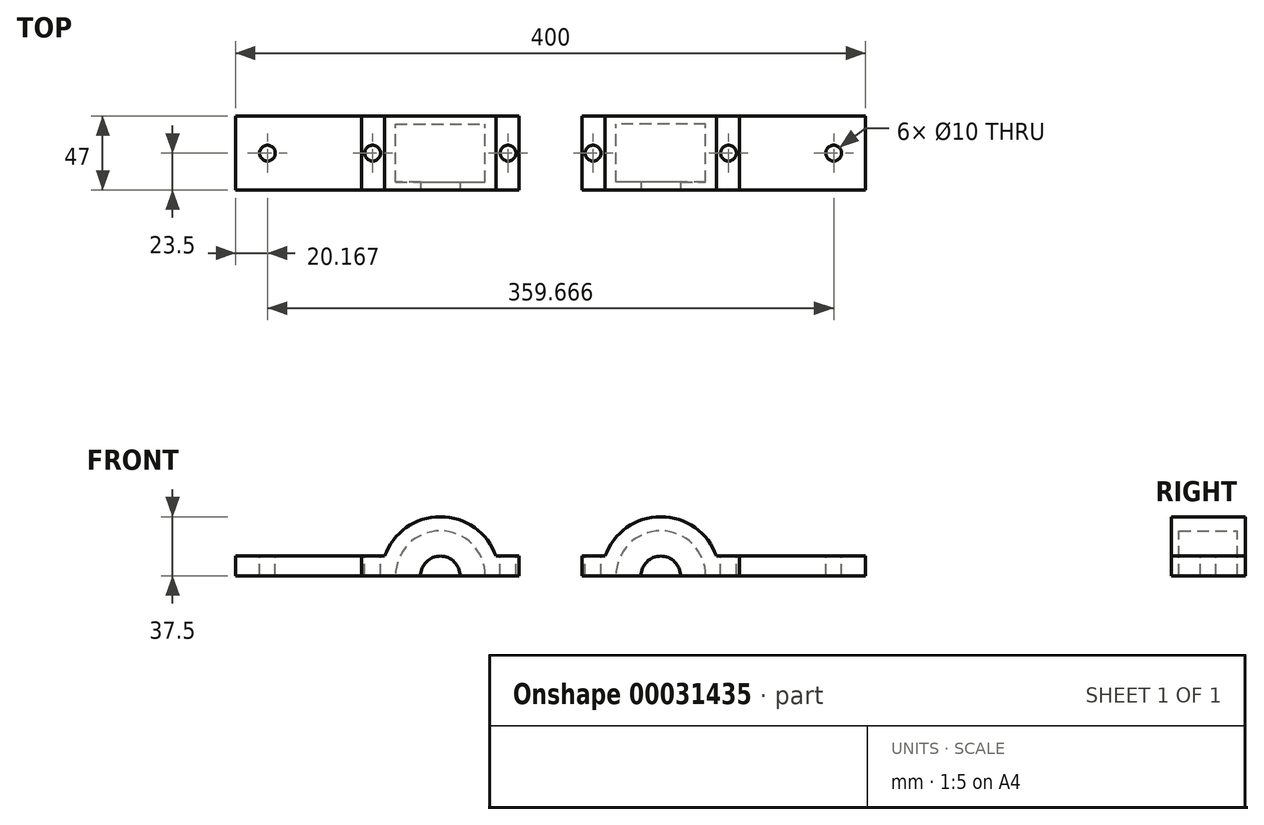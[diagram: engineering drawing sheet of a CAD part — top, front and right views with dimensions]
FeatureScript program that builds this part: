
annotation { "Feature Type Name" : "Feature", "Feature Type Description" : "" }
export const myFeature = defineFeature(function(context is Context, id is Id, definition is map)
    precondition{}
    {
        {
            var Q0;
            Q0=qCreatedBy(makeId("Front.planeOp"),FACE);
            var sketch = newSketch(context, id + "F0", { "sketchPlane" : qUnion([Q0])});
            skLineSegment(sketch, "E0.bottom", {"start": v(0, 0) * mm, "end": v(-50, 0) * mm});
            skLineSegment(sketch, "E0.top", {"start": v(0, 50) * mm, "end": v(-50, 50) * mm});
            skLineSegment(sketch, "E0.left", {"start": v(0, 0) * mm, "end": v(0, 50) * mm});
            skLineSegment(sketch, "E0.right", {"start": v(-50, 0) * mm, "end": v(-50, 50) * mm});
            skArc(sketch, "E1", {"start": v(0, 28.5) * mm, "mid": v(-20.15, 20.15) * mm, "end": v(-28.5, 0) * mm});
            skSolve(sketch);
        }
        {
            var Q0;
            {var subQ3=sQuery(id+"F0.wireOp",EDGE,"E0.top");Q0=makeQuery(id+"F0.imprint","IMPRINT",FACE,{"disambiguationData":[TD([[makeQuery(id+"F0.imprint","IMPRINT",EDGE,{"derivedFrom":subQ3}),1.0]])]});}
            extrude(context, id + "F1", {"entities" : qUnion([Q0]), "depth" : 37 * mm});
        }
        {
            var Q0;
            {var subQ0=sQuery(id+"F0.wireOp",EDGE,"E1");Q0=makeQuery(id+"F0.imprint","IMPRINT",FACE,{"disambiguationData":[TD([[makeQuery(id+"F0.imprint","IMPRINT",EDGE,{"derivedFrom":subQ0}),1.0]])]});}
            var Q1;
            {var subQ3=sQuery(id+"F0.wireOp",EDGE,"E0.top");Q1=makeQuery(id+"F0.imprint","IMPRINT",FACE,{"disambiguationData":[TD([[makeQuery(id+"F0.imprint","IMPRINT",EDGE,{"derivedFrom":subQ3}),1.0]])]});}
            extrude(context, id + "F2", {"entities" : qUnion([Q0, Q1]), "operationType" : NewBodyOperationType.ADD, "oppositeDirection" : true, "depth" : 5 * mm});
        }
        {
            var Q0;
            Q0=qCreatedBy(makeId("Front.planeOp"),FACE);
            cPlane(context, id + "F3", {"entities" : qUnion([Q0]), "cplaneType" : CPlaneType.OFFSET, "offset" : 37 * mm, "width" : 150 * mm, "height" : 150 * mm});
        }
        {
            var Q0;
            Q0=qCreatedBy(id+"F3.planeOp",FACE);
            var sketch = newSketch(context, id + "F4", { "sketchPlane" : qUnion([Q0])});
            skLineSegment(sketch, "E2.bottom", {"start": v(0, 0) * mm, "end": v(-50, 0) * mm});
            skLineSegment(sketch, "E2.top", {"start": v(0, 50) * mm, "end": v(-50, 50) * mm});
            skLineSegment(sketch, "E2.left", {"start": v(0, 0) * mm, "end": v(0, 50) * mm});
            skLineSegment(sketch, "E2.right", {"start": v(-50, 0) * mm, "end": v(-50, 50) * mm});
            skSolve(sketch);
        }
        {
            var Q0;
            Q0 = qSketchRegion(id + "F4", true);
            extrude(context, id + "F5", {"entities" : qUnion([Q0]), "depth" : 5 * mm});
        }
        {
            var Q0;
            Q0=makeQuery(id+"F1.opExtrude","SWEPT_BODY",BODY,{"disambiguationData":[OSD([sQuery(id+"F0.wireOp",EDGE,"E0.bottom"),sQuery(id+"F0.wireOp",EDGE,"E0.top"),sQuery(id+"F0.wireOp",EDGE,"E0.left"),sQuery(id+"F0.wireOp",EDGE,"E0.right"),sQuery(id+"F0.wireOp",EDGE,"E1")])]});
            var Q1;
            Q1=makeQuery(id+"F5.opExtrude","SWEPT_BODY",BODY,{"disambiguationData":[OSD([sQuery(id+"F4.wireOp",EDGE,"E2.bottom"),sQuery(id+"F4.wireOp",EDGE,"E2.top"),sQuery(id+"F4.wireOp",EDGE,"E2.left"),sQuery(id+"F4.wireOp",EDGE,"E2.right")])]});
            booleanBodies(context, id + "F6", {"operationType" : BooleanOperationType.UNION, "tools" : qUnion([Q0, Q1])});
        }
        {
            var Q0;
            {var subQ0=sQuery(id+"F0.wireOp",EDGE,"E0.top");var subQ1=makeQuery(id+"F2.boolean.opBoolean","MERGE",FACE,{"derivedFrom":[makeQuery(id+"F1.opExtrude","SWEPT_FACE",FACE,{"disambiguationData":[OSD([subQ0])]}),makeQuery(id+"F2.opExtrude","SWEPT_FACE",FACE,{"disambiguationData":[OSD([subQ0])]})]});var subQ2=makeQuery(id+"F5.opExtrude","SWEPT_FACE",FACE,{"disambiguationData":[OSD([sQuery(id+"F4.wireOp",EDGE,"E2.top")])]});Q0=makeQuery(id+"F6.opBoolean","MERGE",FACE,{"derivedFrom":[makeQuery(id+"FJoy3nQs1lwyxgx_1.boolean.opBoolean","MERGE",FACE,{"derivedFrom":[subQ1,makeQuery(id+"FJoy3nQs1lwyxgx_1.opPattern","COPY",FACE,{"derivedFrom":subQ1,"instanceName":"1"})]}),makeQuery(id+"Fkg0O5OeTg1i3LZ_2.boolean.opBoolean","MERGE",FACE,{"derivedFrom":[subQ2,makeQuery(id+"Fkg0O5OeTg1i3LZ_2.opPattern","COPY",FACE,{"derivedFrom":subQ2,"instanceName":"1"})]})]});}
            var sketch = newSketch(context, id + "F7", { "sketchPlane" : qUnion([Q0])});
            skCircle(sketch, "E3", {"center": v(-43, -18.5) * mm, "radius": 5 * mm});
            skSolve(sketch);
        }
        {
            var Q0;
            Q0 = qSketchRegion(id + "F7", true);
            extrude(context, id + "F8", {"entities" : qUnion([Q0]), "operationType" : NewBodyOperationType.REMOVE, "oppositeDirection" : true, "depth" : 100 * mm});
        }
        {
            var Q0;
            Q0=makeQuery(id+"F5.opExtrude","CAP_FACE",FACE,{"disambiguationData":[OSD([sQuery(id+"F4.wireOp",EDGE,"E2.bottom"),sQuery(id+"F4.wireOp",EDGE,"E2.top"),sQuery(id+"F4.wireOp",EDGE,"E2.left"),sQuery(id+"F4.wireOp",EDGE,"E2.right")])],"isStart":false});
            var sketch = newSketch(context, id + "F9", { "sketchPlane" : qUnion([Q0])});
            skCircle(sketch, "E4", {"center": v(0, 0) * mm, "radius": 12.5 * mm});
            skSolve(sketch);
        }
        {
            var Q0;
            Q0 = qSketchRegion(id + "F9", true);
            extrude(context, id + "F10", {"entities" : qUnion([Q0]), "operationType" : NewBodyOperationType.REMOVE, "oppositeDirection" : true, "depth" : 5 * mm});
        }
        {
            var Q0;
            Q0=makeQuery(id+"F5.opExtrude","CAP_FACE",FACE,{"disambiguationData":[OSD([sQuery(id+"F4.wireOp",EDGE,"E2.bottom"),sQuery(id+"F4.wireOp",EDGE,"E2.top"),sQuery(id+"F4.wireOp",EDGE,"E2.left"),sQuery(id+"F4.wireOp",EDGE,"E2.right")])],"isStart":false});
            var sketch = newSketch(context, id + "F11", { "sketchPlane" : qUnion([Q0])});
            skLineSegment(sketch, "E5", {"start": v(0, 12.5) * mm, "end": v(-50, 12.5) * mm, "construction": true});
            skCircle(sketch, "E6", {"center": v(0, 0) * mm, "radius": 37.5 * mm});
            skLineSegment(sketch, "E7", {"start": v(-25, 12.5) * mm, "end": v(-50, 12.5) * mm});
            skLineSegment(sketch, "E8", {"start": v(-50, 50) * mm, "end": v(0, 50) * mm});
            skLineSegment(sketch, "E9", {"start": v(0, 50) * mm, "end": v(0, 37.5) * mm});
            skPoint(sketch, "E9.endSnap0", {"position": v(0, 31.25) * mm});
            skLineSegment(sketch, "E10", {"start": v(-35.36, 12.5) * mm, "end": v(-25, 12.5) * mm});
            skSolve(sketch);
        }
        {
            var Q0;
            {var subQ1=sQuery(id+"F11.wireOp",EDGE,"E7");Q0=makeQuery(id+"F11.imprint","IMPRINT",FACE,{"disambiguationData":[TD([[makeQuery(id+"F11.imprint","IMPRINT",EDGE,{"derivedFrom":subQ1}),-1.0]])]});}
            extrude(context, id + "F12", {"entities" : qUnion([Q0]), "operationType" : NewBodyOperationType.REMOVE, "oppositeDirection" : true, "depth" : 55 * mm});
        }
        {
            var Q0;
            Q0=makeQuery(id+"F1.opExtrude","SWEPT_BODY",BODY,{"disambiguationData":[OSD([sQuery(id+"F0.wireOp",EDGE,"E0.bottom"),sQuery(id+"F0.wireOp",EDGE,"E0.top"),sQuery(id+"F0.wireOp",EDGE,"E0.left"),sQuery(id+"F0.wireOp",EDGE,"E0.right"),sQuery(id+"F0.wireOp",EDGE,"E1")])]});
            var Q1;
            Q1=qCreatedBy(makeId("Right.planeOp"),FACE);
            mirror(context, id + "F13", {"operationType" : NewBodyOperationType.ADD, "entities" : qUnion([Q0]), "mirrorPlane" : qUnion([Q1])});
        }
        {
            var Q0;
            {var subQ0=makeQuery(id+"F5.opExtrude","CAP_FACE",FACE,{"disambiguationData":[OSD([sQuery(id+"F4.wireOp",EDGE,"E2.bottom"),sQuery(id+"F4.wireOp",EDGE,"E2.top"),sQuery(id+"F4.wireOp",EDGE,"E2.left"),sQuery(id+"F4.wireOp",EDGE,"E2.right")])],"isStart":false});Q0=makeQuery(id+"F13.boolean.opBoolean","MERGE",FACE,{"derivedFrom":[subQ0,makeQuery(id+"F13.opPattern","COPY",FACE,{"derivedFrom":subQ0,"instanceName":"1"})]});}
            var sketch = newSketch(context, id + "F14", { "sketchPlane" : qUnion([Q0])});
            skLineSegment(sketch, "E11.bottom", {"start": v(50, 12.5) * mm, "end": v(130, 12.5) * mm});
            skLineSegment(sketch, "E11.top", {"start": v(50, 0) * mm, "end": v(130, 0) * mm});
            skLineSegment(sketch, "E11.left", {"start": v(50, 12.5) * mm, "end": v(50, 0) * mm});
            skLineSegment(sketch, "E11.right", {"start": v(130, 12.5) * mm, "end": v(130, 0) * mm});
            skSolve(sketch);
        }
        {
            var Q0;
            Q0 = qSketchRegion(id + "F14", true);
            extrude(context, id + "F15", {"entities" : qUnion([Q0]), "oppositeDirection" : true, "depth" : 47 * mm});
        }
        {
            var Q0;
            Q0=makeQuery(id+"F15.opExtrude","SWEPT_FACE",FACE,{"disambiguationData":[OSD([sQuery(id+"F14.wireOp",EDGE,"E11.bottom")])]});
            var sketch = newSketch(context, id + "F16", { "sketchPlane" : qUnion([Q0])});
            skLineSegment(sketch, "E12", {"start": v(50, -18.5) * mm, "end": v(130, -18.5) * mm, "construction": true});
            skLineSegment(sketch, "E13", {"start": v(109.83, 5) * mm, "end": v(109.83, -42) * mm, "construction": true});
            skCircle(sketch, "E14", {"center": v(109.83, -18.5) * mm, "radius": 5 * mm});
            skSolve(sketch);
        }
        {
            var Q0;
            Q0 = qSketchRegion(id + "F16", true);
            extrude(context, id + "F17", {"entities" : qUnion([Q0]), "operationType" : NewBodyOperationType.REMOVE, "oppositeDirection" : true, "depth" : 25 * mm});
        }
        {
            var Q0;
            Q0=qCreatedBy(makeId("Right.planeOp"),FACE);
            cPlane(context, id + "F18", {"entities" : qUnion([Q0]), "cplaneType" : CPlaneType.OFFSET, "offset" : 70 * mm, "oppositeDirection" : true, "width" : 150 * mm, "height" : 150 * mm});
        }
        {
            var Q0;
            Q0=makeQuery(id+"F1.opExtrude","SWEPT_BODY",BODY,{"disambiguationData":[OSD([sQuery(id+"F0.wireOp",EDGE,"E0.bottom"),sQuery(id+"F0.wireOp",EDGE,"E0.top"),sQuery(id+"F0.wireOp",EDGE,"E0.left"),sQuery(id+"F0.wireOp",EDGE,"E0.right"),sQuery(id+"F0.wireOp",EDGE,"E1")])]});
            var Q1;
            Q1=makeQuery(id+"F15.opExtrude","SWEPT_BODY",BODY,{"disambiguationData":[OSD([sQuery(id+"F14.wireOp",EDGE,"E11.bottom"),sQuery(id+"F14.wireOp",EDGE,"E11.top"),sQuery(id+"F14.wireOp",EDGE,"E11.left"),sQuery(id+"F14.wireOp",EDGE,"E11.right")])]});
            var Q2;
            Q2=qCreatedBy(id+"F18.planeOp",FACE);
            mirror(context, id + "F19", {"entities" : qUnion([Q0, Q1]), "mirrorPlane" : qUnion([Q2])});
        }
    });
